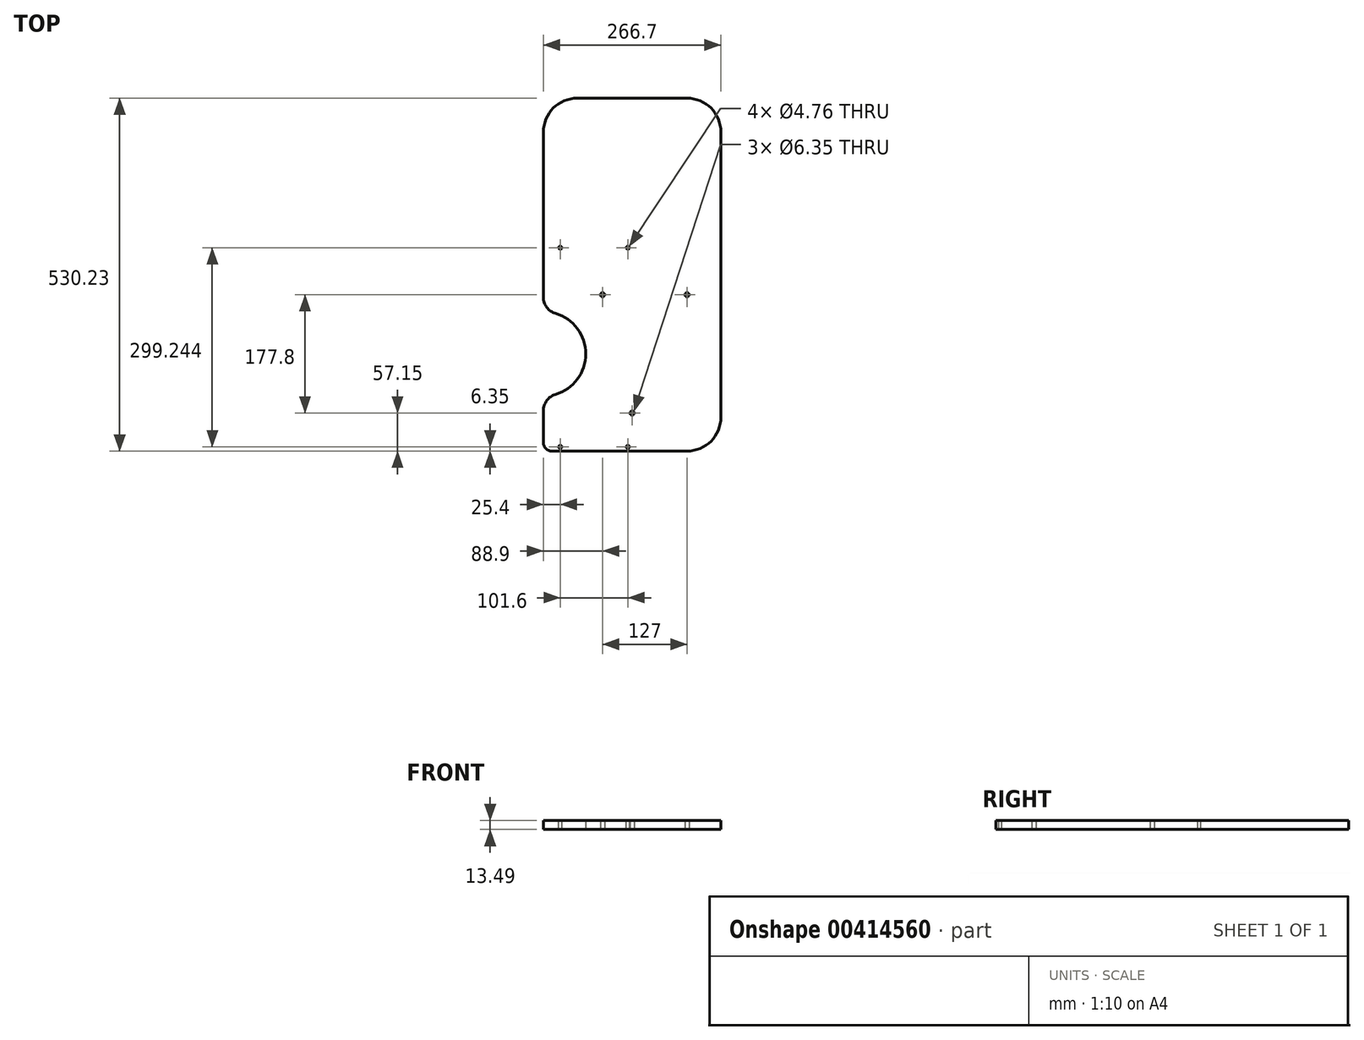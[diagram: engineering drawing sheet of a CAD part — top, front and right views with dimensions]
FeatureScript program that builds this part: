
annotation { "Feature Type Name" : "Feature", "Feature Type Description" : "" }
export const myFeature = defineFeature(function(context is Context, id is Id, definition is map)
    precondition{}
    {
        {
            var Q0;
            Q0=qCreatedBy(makeId("Top.planeOp"),FACE);
            var sketch = newSketch(context, id + "F0", { "sketchPlane" : qUnion([Q0])});
            skCircle(sketch, "E0", {"center": v(-44.45, 88.9) * mm, "radius": 3.18 * mm});
            skCircle(sketch, "E1", {"center": v(82.55, 88.9) * mm, "radius": 3.18 * mm});
            skCircle(sketch, "E2", {"center": v(0, -88.9) * mm, "radius": 3.18 * mm});
            skLineSegment(sketch, "E3", {"start": v(-44.45, 88.9) * mm, "end": v(82.55, 88.9) * mm, "construction": true});
            skLineSegment(sketch, "E4.bottom", {"start": v(133.35, 146.05) * mm, "end": v(-133.35, 146.05) * mm});
            skLineSegment(sketch, "E4.top", {"start": v(133.35, -146.05) * mm, "end": v(-133.35, -146.05) * mm});
            skLineSegment(sketch, "E4.left", {"start": v(133.35, 146.05) * mm, "end": v(133.35, -146.05) * mm});
            skLineSegment(sketch, "E4.right", {"start": v(-133.35, 146.05) * mm, "end": v(-133.35, -146.05) * mm});
            skPoint(sketch, "E4.middle", {"position": v(0, 0) * mm});
            skArc(sketch, "E5", {"start": v(-133.35, -63.5) * mm, "mid": v(-69.85, 0) * mm, "end": v(-133.35, 63.5) * mm});
            skLineSegment(sketch, "E6", {"start": v(19.05, 88.9) * mm, "end": v(19.05, -88.9) * mm, "construction": true});
            skLineSegment(sketch, "E7", {"start": v(0, 0) * mm, "end": v(19.05, 0) * mm, "construction": true});
            skSolve(sketch);
        }
        {
            var Q0;
            Q0=makeQuery(id+"F0.imprint","IMPRINT",FACE,{"disambiguationData":[TD([[makeQuery(id+"F0.imprint","IMPRINT",EDGE,{"derivedFrom":sQuery(id+"F0.wireOp",EDGE,"E0")}),-1.0]])]});
            extrude(context, id + "F1", {"entities" : qUnion([Q0]), "depth" : 13.5 * mm});
        }
        {
            var Q0;
            {var subQ0=sQuery(id+"F0.wireOp",EDGE,"E5");var subQ1=sQuery(id+"F0.wireOp",EDGE,"E4.right");Q0=makeQuery(id+"F1.opExtrude","SWEPT_EDGE",EDGE,{"disambiguationData":[OSD([subQ1,subQ0]),TDD([makeQuery(id+"F0.imprint","INTERSECT",VERTEX,{"disambiguationData":[OD(1.0)],"derivedFrom":[subQ1,subQ0]})])]});}
            var Q1;
            {var subQ0=sQuery(id+"F0.wireOp",EDGE,"E5");var subQ1=sQuery(id+"F0.wireOp",EDGE,"E4.right");Q1=makeQuery(id+"F1.opExtrude","SWEPT_EDGE",EDGE,{"disambiguationData":[OSD([subQ1,subQ0]),TDD([makeQuery(id+"F0.imprint","INTERSECT",VERTEX,{"disambiguationData":[OD(0.0)],"derivedFrom":[subQ1,subQ0]})])]});}
            fillet(context, id + "F2", {"entities" : qUnion([Q0, Q1]), "radius" : 25.4 * mm, "tangentPropagation" : true, "allowEdgeOverflow" : false});
        }
        {
            var Q0;
            Q0=makeQuery(id+"F1.opExtrude","CAP_FACE",FACE,{"disambiguationData":[OSD([sQuery(id+"F0.wireOp",EDGE,"E0"),sQuery(id+"F0.wireOp",EDGE,"E1"),sQuery(id+"F0.wireOp",EDGE,"E2"),sQuery(id+"F0.wireOp",EDGE,"E4.bottom"),sQuery(id+"F0.wireOp",EDGE,"E4.top"),sQuery(id+"F0.wireOp",EDGE,"E4.left"),sQuery(id+"F0.wireOp",EDGE,"E4.right"),sQuery(id+"F0.wireOp",EDGE,"E5")])],"isStart":false});
            var sketch = newSketch(context, id + "F3", { "sketchPlane" : qUnion([Q0])});
            skCircle(sketch, "E8", {"center": v(-107.95, -139.7) * mm, "radius": 2.38 * mm});
            skCircle(sketch, "E9", {"center": v(-6.35, -139.7) * mm, "radius": 2.38 * mm});
            skLineSegment(sketch, "E10", {"start": v(-6.35, -139.7) * mm, "end": v(-6.35, 159.54) * mm, "construction": true});
            skLineSegment(sketch, "E11", {"start": v(-107.95, -139.7) * mm, "end": v(-107.95, 159.54) * mm, "construction": true});
            skCircle(sketch, "E12", {"center": v(-6.35, 159.54) * mm, "radius": 2.38 * mm});
            skCircle(sketch, "E13", {"center": v(-107.95, 159.54) * mm, "radius": 2.38 * mm});
            skSolve(sketch);
        }
        {
            var Q0;
            Q0=makeQuery(id+"F1.opExtrude","CAP_FACE",FACE,{"disambiguationData":[OSD([sQuery(id+"F0.wireOp",EDGE,"E0"),sQuery(id+"F0.wireOp",EDGE,"E1"),sQuery(id+"F0.wireOp",EDGE,"E2"),sQuery(id+"F0.wireOp",EDGE,"E4.bottom"),sQuery(id+"F0.wireOp",EDGE,"E4.top"),sQuery(id+"F0.wireOp",EDGE,"E4.left"),sQuery(id+"F0.wireOp",EDGE,"E4.right"),sQuery(id+"F0.wireOp",EDGE,"E5")])],"isStart":false});
            var sketch = newSketch(context, id + "F4", { "sketchPlane" : qUnion([Q0])});
            skLineSegment(sketch, "E14.bottom", {"start": v(-133.35, 146.05) * mm, "end": v(133.35, 146.05) * mm});
            skLineSegment(sketch, "E14.top", {"start": v(-133.35, 384.18) * mm, "end": v(133.35, 384.18) * mm});
            skLineSegment(sketch, "E14.left", {"start": v(-133.35, 146.05) * mm, "end": v(-133.35, 384.18) * mm});
            skLineSegment(sketch, "E14.right", {"start": v(133.35, 146.05) * mm, "end": v(133.35, 384.18) * mm});
            skSolve(sketch);
        }
        {
            var Q0;
            Q0=makeQuery(id+"F4.imprint","IMPRINT",FACE,{"disambiguationData":[TD([[makeQuery(id+"F4.imprint","IMPRINT",EDGE,{"derivedFrom":sQuery(id+"F4.wireOp",EDGE,"E14.bottom")}),-1.0]])]});
            var Q1;
            Q1=makeQuery(id+"F1.opExtrude","CAP_FACE",FACE,{"disambiguationData":[OSD([sQuery(id+"F0.wireOp",EDGE,"E0"),sQuery(id+"F0.wireOp",EDGE,"E1"),sQuery(id+"F0.wireOp",EDGE,"E2"),sQuery(id+"F0.wireOp",EDGE,"E4.bottom"),sQuery(id+"F0.wireOp",EDGE,"E4.top"),sQuery(id+"F0.wireOp",EDGE,"E4.left"),sQuery(id+"F0.wireOp",EDGE,"E4.right"),sQuery(id+"F0.wireOp",EDGE,"E5")])],"isStart":true});
            extrude(context, id + "F5", {"entities" : qUnion([Q0]), "operationType" : NewBodyOperationType.ADD, "endBound" : BoundingType.UP_TO_SURFACE, "oppositeDirection" : true, "endBoundEntityFace" : qUnion([Q1]), "depth" : 25.4 * mm});
        }
        {
            var Q0;
            Q0 = qSketchRegion(id + "F3", true);
            extrude(context, id + "F6", {"entities" : qUnion([Q0]), "operationType" : NewBodyOperationType.REMOVE, "endBound" : BoundingType.THROUGH_ALL, "oppositeDirection" : true, "depth" : 25.4 * mm});
        }
        {
            var Q0;
            Q0=makeQuery(id+"F1.opExtrude","SWEPT_EDGE",EDGE,{"disambiguationData":[OSD([sQuery(id+"F0.wireOp",EDGE,"E4.top"),sQuery(id+"F0.wireOp",EDGE,"E4.left")])]});
            var Q1;
            Q1=makeQuery(id+"F5.opExtrude","SWEPT_EDGE",EDGE,{"disambiguationData":[OSD([sQuery(id+"F4.wireOp",EDGE,"E14.top"),sQuery(id+"F4.wireOp",EDGE,"E14.right")])]});
            var Q2;
            Q2=makeQuery(id+"F5.opExtrude","SWEPT_EDGE",EDGE,{"disambiguationData":[OSD([sQuery(id+"F4.wireOp",EDGE,"E14.top"),sQuery(id+"F4.wireOp",EDGE,"E14.left")])]});
            fillet(context, id + "F7", {"entities" : qUnion([Q0, Q1, Q2]), "radius" : 50.8 * mm, "tangentPropagation" : true, "allowEdgeOverflow" : false});
        }
        {
            var Q0;
            Q0=makeQuery(id+"F1.opExtrude","SWEPT_EDGE",EDGE,{"disambiguationData":[OSD([sQuery(id+"F0.wireOp",EDGE,"E4.top"),sQuery(id+"F0.wireOp",EDGE,"E4.right")])]});
            fillet(context, id + "F8", {"entities" : qUnion([Q0]), "radius" : 12.7 * mm, "tangentPropagation" : true, "allowEdgeOverflow" : false});
        }
    });
